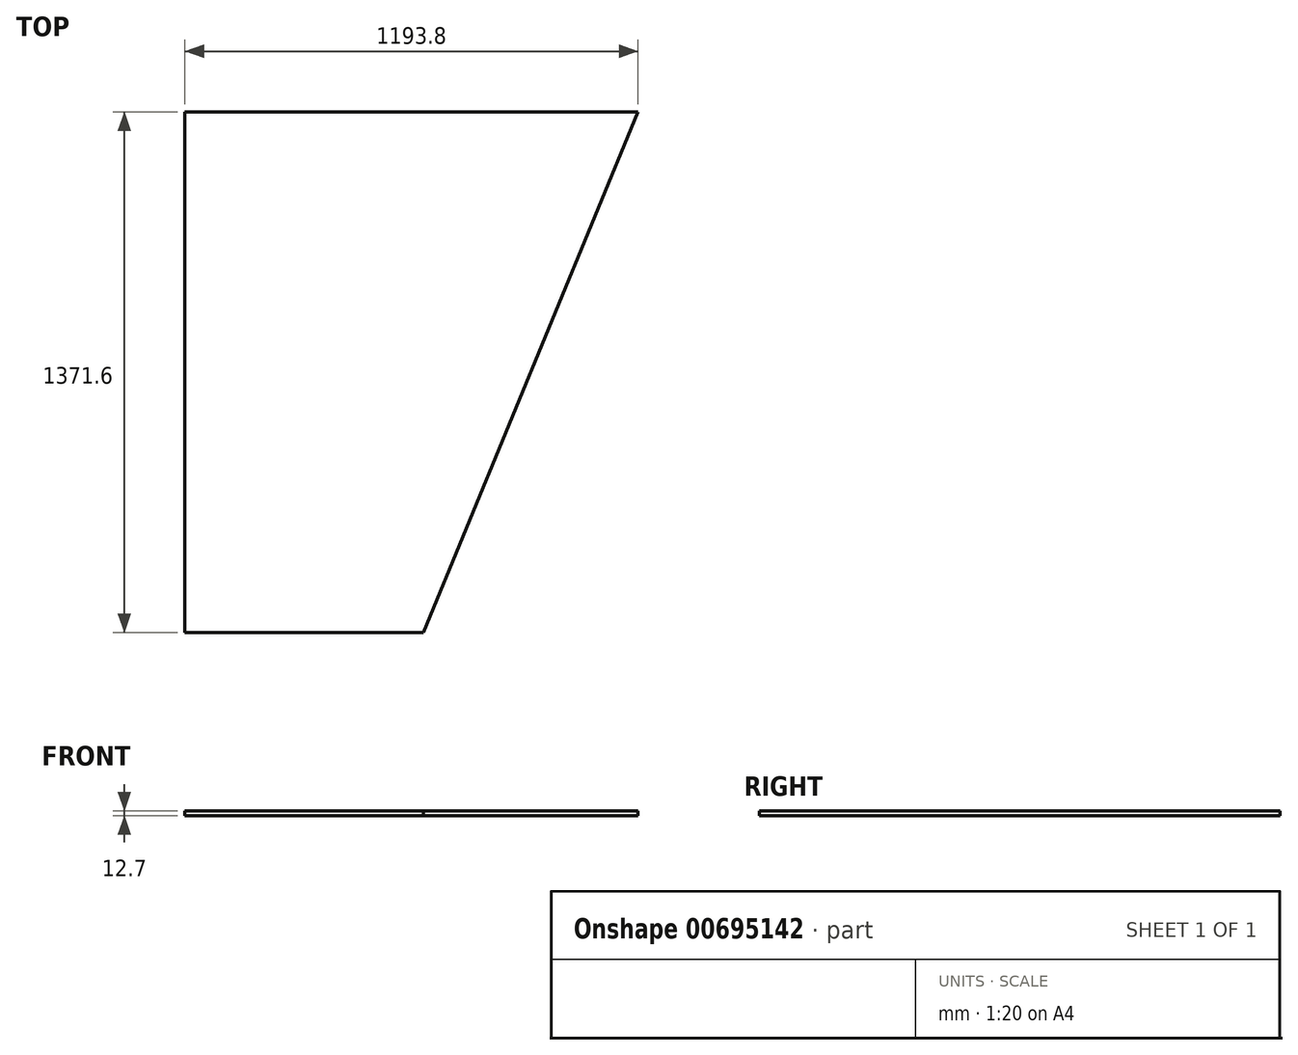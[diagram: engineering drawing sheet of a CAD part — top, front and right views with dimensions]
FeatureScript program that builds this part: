
annotation { "Feature Type Name" : "Feature", "Feature Type Description" : "" }
export const myFeature = defineFeature(function(context is Context, id is Id, definition is map)
    precondition{}
    {
        {
            var Q0;
            Q0=qCreatedBy(makeId("Top.planeOp"),FACE);
            var sketch = newSketch(context, id + "F0", { "sketchPlane" : qUnion([Q0])});
            skLineSegment(sketch, "E0", {"start": v(139.03, 2617.97) * mm, "end": v(767.68, 2617.97) * mm});
            skLineSegment(sketch, "E1", {"start": v(767.68, 2617.97) * mm, "end": v(1332.83, 3989.57) * mm});
            skLineSegment(sketch, "E2", {"start": v(1332.83, 3989.57) * mm, "end": v(139.03, 3989.57) * mm});
            skLineSegment(sketch, "E3", {"start": v(139.03, 3989.57) * mm, "end": v(139.03, 2617.97) * mm});
            skSolve(sketch);
        }
        {
            var Q0;
            Q0=makeQuery(id+"F0.imprint","IMPRINT",FACE,{"disambiguationData":[TD([[makeQuery(id+"F0.imprint","IMPRINT",EDGE,{"derivedFrom":sQuery(id+"F0.wireOp",EDGE,"E0")}),1.0]])]});
            extrude(context, id + "F1", {"entities" : qUnion([Q0]), "depth" : 12.7 * mm, "offsetDistance" : 25.4 * mm});
        }
    });
